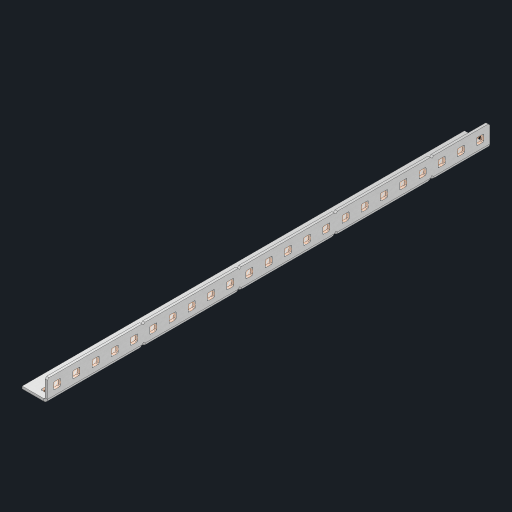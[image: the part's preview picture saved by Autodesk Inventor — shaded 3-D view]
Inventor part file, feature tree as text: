
AUTODESK INVENTOR PART (.ipt)
format: ipt  version: 2023 (Build 270158000, 158)  size: 828,928 bytes
history: native  units: in
note: dims shown in document units (in); Inventor stores cm internally (conversion verified against a paired STEP export)
features: other x51, extrude x45, sheet_metal_op x10, sketch x8, mirror x1, pattern_linear x1, chamfer x1
ambient origin geometry x8: Origin, YZ Plane, XZ Plane, XY Plane, X Axis, Y Axis, Z Axis, Center Point
bodies: Solid1 (feature_tree), Body (feature_tree)
feature tree (117):
  other  "Flange Pattern Plane"
  sheet_metal_op  "Flange Pattern"
  sheet_metal_op  "Body Pattern"
  other  "Arc Length"
  mirror  "Notch Mirror"
  pattern_linear  "Notch Pattern"  Spacing1=0.25in  [1 undecoded]
  chamfer  "End Chamfer"
  extrude  "Half Cut"  Depth=0.0625in
  sketch  "Sketch1"  dims[d0=1.5in]
  other  "Plate1"
  sketch  "Sketch2"  dims[d1=11.5in]
  other  "Plate2"
  sheet_metal_op  "Bend1"
  sheet_metal_op  "Corner1"
  sketch  "Sketch3"  dims[d2=0.0625in]
  other  "Flange Pattern Sketch"
  sketch  "Sketch7"  dims[d3=0.0625in]
  other  "Srf1"
  other  "Srf2"
  sketch  "Sketch8"  dims[d4=0.0312in]
  sketch  "Sketch9"  dims[d5=0.125in]
  other  "Srf91"
  sheet_metal_op  "Body Pattern Sketch"
  other  "Srf92"
  sketch  "Sketch13"  dims[d6=0.0625in]
  sketch  "Sketch14"  dims[d7=0.5in d8=90.0deg d9=0.0312in d10=0.25in d11=0.0625in d12=0.0625in d16=0.182in d17=0.02in d18=0.0625in d19=0.0in d20=0.25in d21=0.25in d46=0.172in d47=1.0in d48=0.0in d49=0.182in d50=0.02in d51=0.25in d52=0.25in d53=0.0625in d54=0.0in d55=0.172in d56=1.0in d57=0.0in d60=9.0551in d62=0.5in d63=0.3937in d65=0.5in d85=0.1473in d86=0.1782in d88=0.04in d89=0.0625in d90=0.0in d91=0.04in d92=0.0491in d95=2.5in d96=0.04in d97=0.25in d98=45.0deg d101=0.0in d102=2.497in d131=0.5in d132=9.0551in d134=0.5in d139=0.5in]
  other  "Srf856"
  other  "Srf1310"
  other  "Srf1311"
  other  "Srf1312"
  other  "Srf1376"
  other  "Srf1377"
  other  "Srf1728"
  other  "Srf1755"
  other  "Srf1878"
  other  "Srf1879"
  other  "Srf1880"
  other  "Srf1881"
  other  "Srf1882"
  other  "Srf1883"
  other  "Srf1884"
  other  "Srf1885"
  other  "Srf1886"
  other  "Srf1887"
  other  "Srf1888"
  other  "Srf1889"
  other  "Srf1890"
  other  "Srf1891"
  other  "Srf1892"
  other  "Srf1893"
  other  "Srf1894"
  other  "Srf1942"
  other  "Srf1943"
  other  "Srf1944"
  other  "Srf1945"
  other  "Srf1946"
  other  "Srf1947"
  other  "Srf1948"
  other  "Srf1949"
  other  "Srf1950"
  other  "Srf1951"
  other  "Srf1952"
  other  "Srf1953"
  other  "Srf1954"
  other  "Srf1955"
  other  "Srf1956"
  other  "Srf1957"
  other  "Srf1958"
  sheet_metal_op  "Flange Stamp"
  sheet_metal_op  "Flange Circle"
  sheet_metal_op  "Body Stamp"
  sheet_metal_op  "Body Circle"
  sheet_metal_op  "Notch"
  extrude  "ExtrusionSrf2"  Depth=0.0625in
  extrude  "ExtrusionSrf92"  Depth=0.5in
  extrude  "ExtrusionSrf856"  Depth=0.02in
  extrude  "ExtrusionSrf1310"  Depth=0.0625in
  extrude  "ExtrusionSrf1311"  TaperAngle=0.0deg  [1 undecoded]
  extrude  "ExtrusionSrf1312"  Depth=0.5in
  extrude  "ExtrusionSrf1376"  Depth=0.5in
  extrude  "ExtrusionSrf1377"  Depth=0.5in
  extrude  "ExtrusionSrf1728"  Depth=0.5in TaperAngle=0.0deg
  extrude  "ExtrusionSrf1755"  Depth=0.5in
  extrude  "ExtrusionSrf1878"  Depth=0.02in
  extrude  "ExtrusionSrf1879"  Depth=0.5in
  extrude  "ExtrusionSrf1880"  Depth=0.5in
  extrude  "ExtrusionSrf1881"  Depth=0.0625in
  extrude  "ExtrusionSrf1882"  TaperAngle=0.0deg  [1 undecoded]
  extrude  "ExtrusionSrf1883"  Depth=0.5in
  extrude  "ExtrusionSrf1884"  Depth=0.5in TaperAngle=0.0deg
  extrude  "ExtrusionSrf1885"  Depth=0.5in
  extrude  "ExtrusionSrf1886"  Depth=0.5in
  extrude  "ExtrusionSrf1887"  Depth=0.5in
  extrude  "ExtrusionSrf1888"  Depth=0.5in
  extrude  "ExtrusionSrf1889"  Depth=0.5in
  extrude  "ExtrusionSrf1890"  Depth=0.0625in
  extrude  "ExtrusionSrf1891"  TaperAngle=0.0deg  [1 undecoded]
  extrude  "ExtrusionSrf1892"  Depth=0.5in
  extrude  "ExtrusionSrf1893"  Depth=0.5in
  extrude  "ExtrusionSrf1894"  Depth=0.5in
  extrude  "ExtrusionSrf1942"  Depth=0.5in TaperAngle=45.0deg
  extrude  "ExtrusionSrf1943"  TaperAngle=0.0deg  [1 undecoded]
  extrude  "ExtrusionSrf1944"  Depth=0.5in
  extrude  "ExtrusionSrf1945"  Depth=0.5in
  extrude  "ExtrusionSrf1946"  Depth=0.5in
  extrude  "ExtrusionSrf1947"  Depth=0.5in
  extrude  "ExtrusionSrf1948"  Depth=0.5in
  extrude  "ExtrusionSrf1949"  [1 undecoded]
  extrude  "ExtrusionSrf1950"  [1 undecoded]
  extrude  "ExtrusionSrf1951"  [1 undecoded]
  extrude  "ExtrusionSrf1952"  [1 undecoded]
  extrude  "ExtrusionSrf1953"  [1 undecoded]
  extrude  "ExtrusionSrf1954"  [1 undecoded]
  extrude  "ExtrusionSrf1955"  [1 undecoded]
  extrude  "ExtrusionSrf1956"  [1 undecoded]
  extrude  "ExtrusionSrf1957"  [1 undecoded]
  extrude  "ExtrusionSrf1958"  [1 undecoded]
note: 15 required parameter values undecoded (feature->parameter linkage not recoverable at this tier; creation-order binding heuristic only, values carry confidence <= 0.55)
